# Revit family: FP-Revit19-en-RS6009V2RT1-RS6009V2R1-RS6009SBLT1-RS6009SBL1-integrated-refrigerator-0-90003378A
name_source: partatom
category: Specialty Equipment
units: mm (PartAtom-declared; Revit-internal decimal feet)

## family parameters
Always vertical = Yes
Cut with Voids When Loaded = Yes
OmniClass Number = 23.40.40.11.11
OmniClass Title = Refrigerators and Freezers
Part Type = Normal
Room Calculation Point = No
Round Connector Dimension = Use Diameter
Shared = No
Work Plane-Based = No

## types (4) — shared parameters
Cavity - Depth (600mm min with services external) = 600 mm  [stored 1.9685 ft]
Cavity - Width = 600 mm  [stored 1.9685 ft]
Connector Description - Electrical = 230 V, 50 Hz, 10 A circuit
Manufacturer = Fisher & Paykel Appliances
Material - Body = Fisher & Paykel - Grey
Material - Door Structure = Fisher & Paykel - White
Panel - Height = 771 mm  [stored 2.52953 ft]
Product - Depth (exl front panel) = 579 mm  [stored 1.89961 ft]
Product - Width = 592 mm  [stored 1.94226 ft]
URL = www.fisherpaykel.com

## per-type parameters (varying)
| type | Description | Handle Offset |
| RS6009V2RT1 | 60cm Integrated Wine Cabinet | 529 mm  [stored 1.73556 ft] |
| RS6009SBL1 | 60cm Integrated Beverage Centre | 63 mm |
| RS6009V2R1 | 60cm Integrated Wine Cabinet | 529 mm  [stored 1.73556 ft] |
| RS6009SBLT1 | 60cm Integrated Beverage Centre | 63 mm |

note: column(s) folded — value = type name in every type: Model

note: [stored X ft] marks values corroborated as IEEE doubles in the binary element streams (Revit-internal decimal feet)

## geometry (parser evidence)
native form markers: Sweep x14
no freeform markers — native parametric forms only
